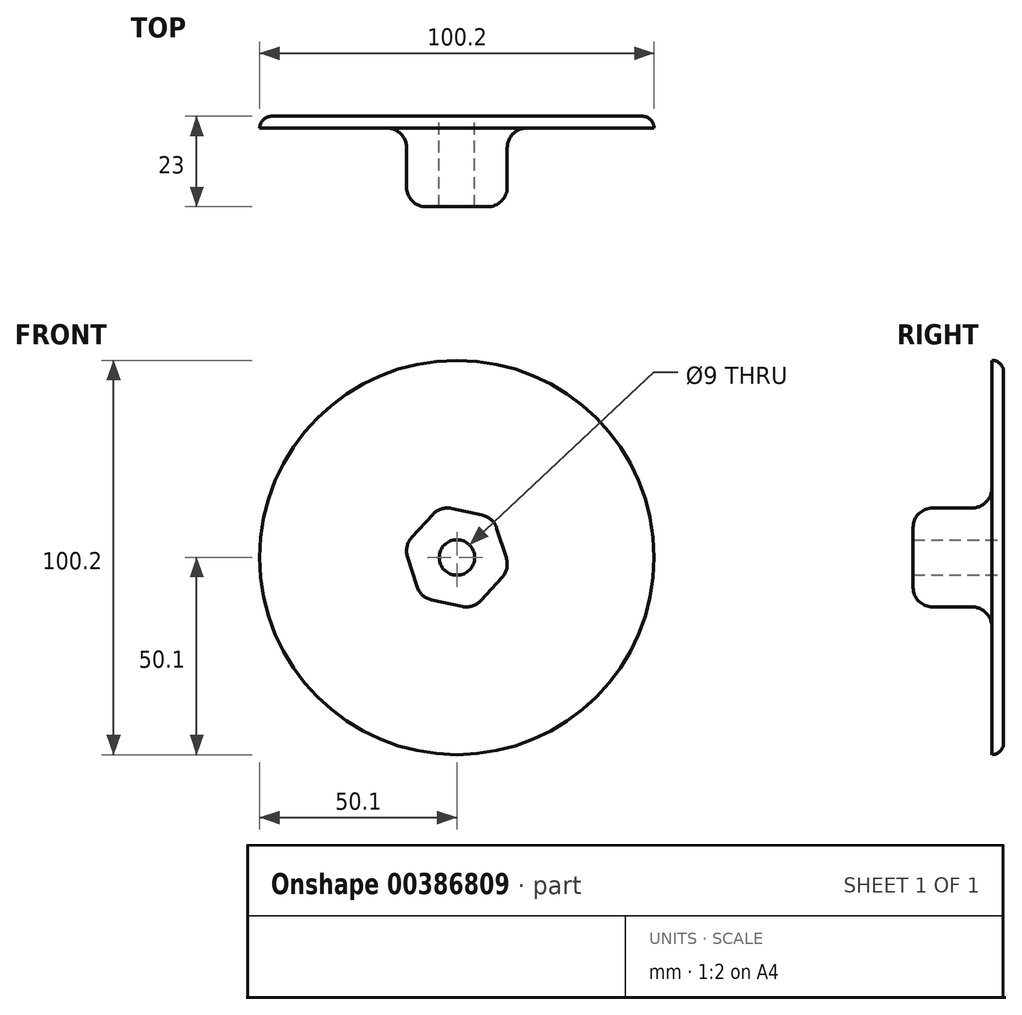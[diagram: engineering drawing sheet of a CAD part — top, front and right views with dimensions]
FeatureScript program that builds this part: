
annotation { "Feature Type Name" : "Feature", "Feature Type Description" : "" }
export const myFeature = defineFeature(function(context is Context, id is Id, definition is map)
    precondition{}
    {
        {
            var Q0;
            Q0=qCreatedBy(makeId("Front.planeOp"),FACE);
            var sketch = newSketch(context, id + "F0", { "sketchPlane" : qUnion([Q0])});
            skCircle(sketch, "E0", {"center": v(0, 0) * mm, "radius": 50.1 * mm});
            skCircle(sketch, "E1", {"center": v(0, 0) * mm, "radius": 4.5 * mm});
            skSolve(sketch);
        }
        {
            var Q0;
            Q0=makeQuery(id+"F0.imprint","IMPRINT",FACE,{"disambiguationData":[TD([[makeQuery(id+"F0.imprint","IMPRINT",EDGE,{"derivedFrom":sQuery(id+"F0.wireOp",EDGE,"E0")}),1.0]])]});
            extrude(context, id + "F1", {"entities" : qUnion([Q0]), "depth" : 3 * mm});
        }
        {
            var Q0;
            Q0=makeQuery(id+"F1.opExtrude","CAP_FACE",FACE,{"disambiguationData":[OSD([sQuery(id+"F0.wireOp",EDGE,"E0"),sQuery(id+"F0.wireOp",EDGE,"E1")])],"isStart":false});
            var sketch = newSketch(context, id + "F2", { "sketchPlane" : qUnion([Q0])});
            skCircle(sketch, "E2.cCircle", {"center": v(0, 0) * mm, "radius": 11.9 * mm, "construction": true});
            skLineSegment(sketch, "E2.0", {"start": v(-4.18, 13.09) * mm, "end": v(9.24, 10.17) * mm});
            skLineSegment(sketch, "E2.1", {"start": v(9.24, 10.17) * mm, "end": v(13.42, -2.92) * mm});
            skLineSegment(sketch, "E2.2", {"start": v(13.42, -2.92) * mm, "end": v(4.18, -13.09) * mm});
            skLineSegment(sketch, "E2.3", {"start": v(4.18, -13.09) * mm, "end": v(-9.24, -10.17) * mm});
            skLineSegment(sketch, "E2.4", {"start": v(-9.24, -10.17) * mm, "end": v(-13.42, 2.92) * mm});
            skLineSegment(sketch, "E2.5", {"start": v(-13.42, 2.92) * mm, "end": v(-4.18, 13.09) * mm});
            skPoint(sketch, "E2.0.midPoint", {"position": v(2.53, 11.63) * mm});
            skCircle(sketch, "E3", {"center": v(0, 0) * mm, "radius": 4.5 * mm});
            skSolve(sketch);
        }
        {
            var Q0;
            Q0=makeQuery(id+"F2.imprint","IMPRINT",FACE,{"disambiguationData":[TD([[makeQuery(id+"F2.imprint","IMPRINT",EDGE,{"derivedFrom":sQuery(id+"F2.wireOp",EDGE,"E2.0")}),-1.0]])]});
            extrude(context, id + "F3", {"entities" : qUnion([Q0]), "operationType" : NewBodyOperationType.ADD, "depth" : 20 * mm});
        }
        {
            var Q0;
            Q0=makeQuery(id+"F1.opExtrude","CAP_EDGE",EDGE,{"disambiguationData":[OSD([sQuery(id+"F0.wireOp",EDGE,"E0")])],"isStart":true});
            fillet(context, id + "F4", {"entities" : qUnion([Q0]), "radius" : 3 * mm, "tangentPropagation" : true, "allowEdgeOverflow" : false});
        }
        {
            var Q0;
            Q0=makeQuery(id+"F3.opExtrude","SWEPT_EDGE",EDGE,{"disambiguationData":[OSD([sQuery(id+"F2.wireOp",EDGE,"E2.0"),sQuery(id+"F2.wireOp",EDGE,"E2.5")])]});
            var Q1;
            Q1=makeQuery(id+"F3.opExtrude","SWEPT_EDGE",EDGE,{"disambiguationData":[OSD([sQuery(id+"F2.wireOp",EDGE,"E2.0"),sQuery(id+"F2.wireOp",EDGE,"E2.1")])]});
            var Q2;
            Q2=makeQuery(id+"F3.opExtrude","SWEPT_EDGE",EDGE,{"disambiguationData":[OSD([sQuery(id+"F2.wireOp",EDGE,"E2.1"),sQuery(id+"F2.wireOp",EDGE,"E2.2")])]});
            var Q3;
            Q3=makeQuery(id+"F3.opExtrude","SWEPT_EDGE",EDGE,{"disambiguationData":[OSD([sQuery(id+"F2.wireOp",EDGE,"E2.2"),sQuery(id+"F2.wireOp",EDGE,"E2.3")])]});
            var Q4;
            Q4=makeQuery(id+"F3.opExtrude","SWEPT_EDGE",EDGE,{"disambiguationData":[OSD([sQuery(id+"F2.wireOp",EDGE,"E2.3"),sQuery(id+"F2.wireOp",EDGE,"E2.4")])]});
            var Q5;
            Q5=makeQuery(id+"F3.opExtrude","SWEPT_EDGE",EDGE,{"disambiguationData":[OSD([sQuery(id+"F2.wireOp",EDGE,"E2.4"),sQuery(id+"F2.wireOp",EDGE,"E2.5")])]});
            fillet(context, id + "F5", {"entities" : qUnion([Q0, Q1, Q2, Q3, Q4, Q5]), "radius" : 5 * mm, "tangentPropagation" : true, "allowEdgeOverflow" : false});
        }
        {
            var Q0;
            Q0=makeQuery(id+"F3.opExtrude","SWEPT_FACE",FACE,{"disambiguationData":[OSD([sQuery(id+"F2.wireOp",EDGE,"E2.1")])]});
            fillet(context, id + "F6", {"entities" : qUnion([Q0]), "radius" : 5 * mm, "tangentPropagation" : true, "allowEdgeOverflow" : false});
        }
    });
